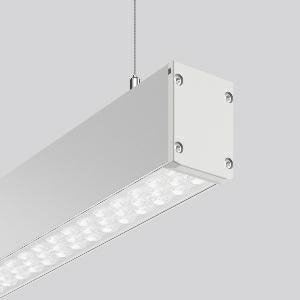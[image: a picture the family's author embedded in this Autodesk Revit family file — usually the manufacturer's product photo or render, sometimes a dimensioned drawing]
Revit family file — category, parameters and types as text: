
# Revit family: linedo_single_ip54_312566_000_1_1963
name_source: partatom
category: Lighting Fixtures
units: mm (PartAtom-declared; Revit-internal decimal feet)

## family parameters
Cut with Voids When Loaded = No
Host = Face
Light Source = No
Part Type = Normal
Room Calculation Point = No
Round Connector Dimension = Use Diameter
Shared = No

## types (1)
- LINEDO single IP54 (1 x LED Modul 840, 6450 lm, 4000)
    Apparent Load = 40 VA
    CIE Flux Codes = 86 96 99 100 100
    Color Rendering = 80
    Color Temperature = 4000
    Default Elevation = 1800 mm
    Description = Series: LINEDO single IP54
Stylish pendant luminaire. High-efficiency LED units with optimum light control thanks to clear plastic (PC) lens optics. 2-point steel cable suspension freely positionable and infinitely height-adjustable. With power cord (2.5 m). Please order canopy separately if required. Perfect for office areas (RUG < 19) and environments with computer screens in accordance with EN 12464-1. Luminaire with limited surface temperature in accordance with EN 60598-2-24 for use in environments in which a deposit of conductive dust on the luminaire can be expected. 
Colour: anodised aluminium
Length: 2274 mm
Width: 58 mm
Height: 76 mm
Suspension length: 100-1500 mm
Lamp: LED
Socket: without socket
Colour temperature: 4000K
Colour rendering index (CRI): 80
System power: 40 W
Rated luminous flux: 6450 lm
Beam angle Down: 59°
Luminous efficiency: 161 lm/W
Control gear: Regulated power supply
Protection class: I
Type of protection: IP 54
    Height = 76 mm
    Lamp = 1 x LED Modul 840
    Lamp Light Flux = 6450 lm
    Lamp count = 1
    Length = 2274 mm
    Lifetime = 50000 h
    Luminous efficacy = 161 lm/W
    Manufacturer = RZB
    ModVariant = No
    Model = 312566.000.1
    Mounting Place = Ceiling
    Mounting Type = Pendant
    Number of Poles = 1
    OnlyDefault = Yes
    Power Factor = 1
    Product Name = LINEDO single IP54
    Product group = Pendant luminaires
    ProductGroupID = 902
    Protection Class = Protection class I
    Protection Degree = Degree of protection
    RLX_Detail_Level = 1
    RLX_Emergency_Light_Flux = 0 lm
    RLX_Emergency_Type = 0
    RLX_Emergency_Type_DB = No
    RlxData = <blob elided: 30785 chars, md5=6f9edc19>
    Socket = socket
    Standby Power = 0 W
    System Light Flux = 6450 lm
    System Power = 40 W
    Type Comments = ALEA SPOT
    Type Image = 312565.000.jpg
    URL = http://relux.com
    VarID = ---
    Voltage = 0 V
    Weight = 0.00 kg
    Width = 58 mm

## geometry (parser evidence)
native form markers: Blend x4, Sweep x10
no freeform markers — native parametric forms only
